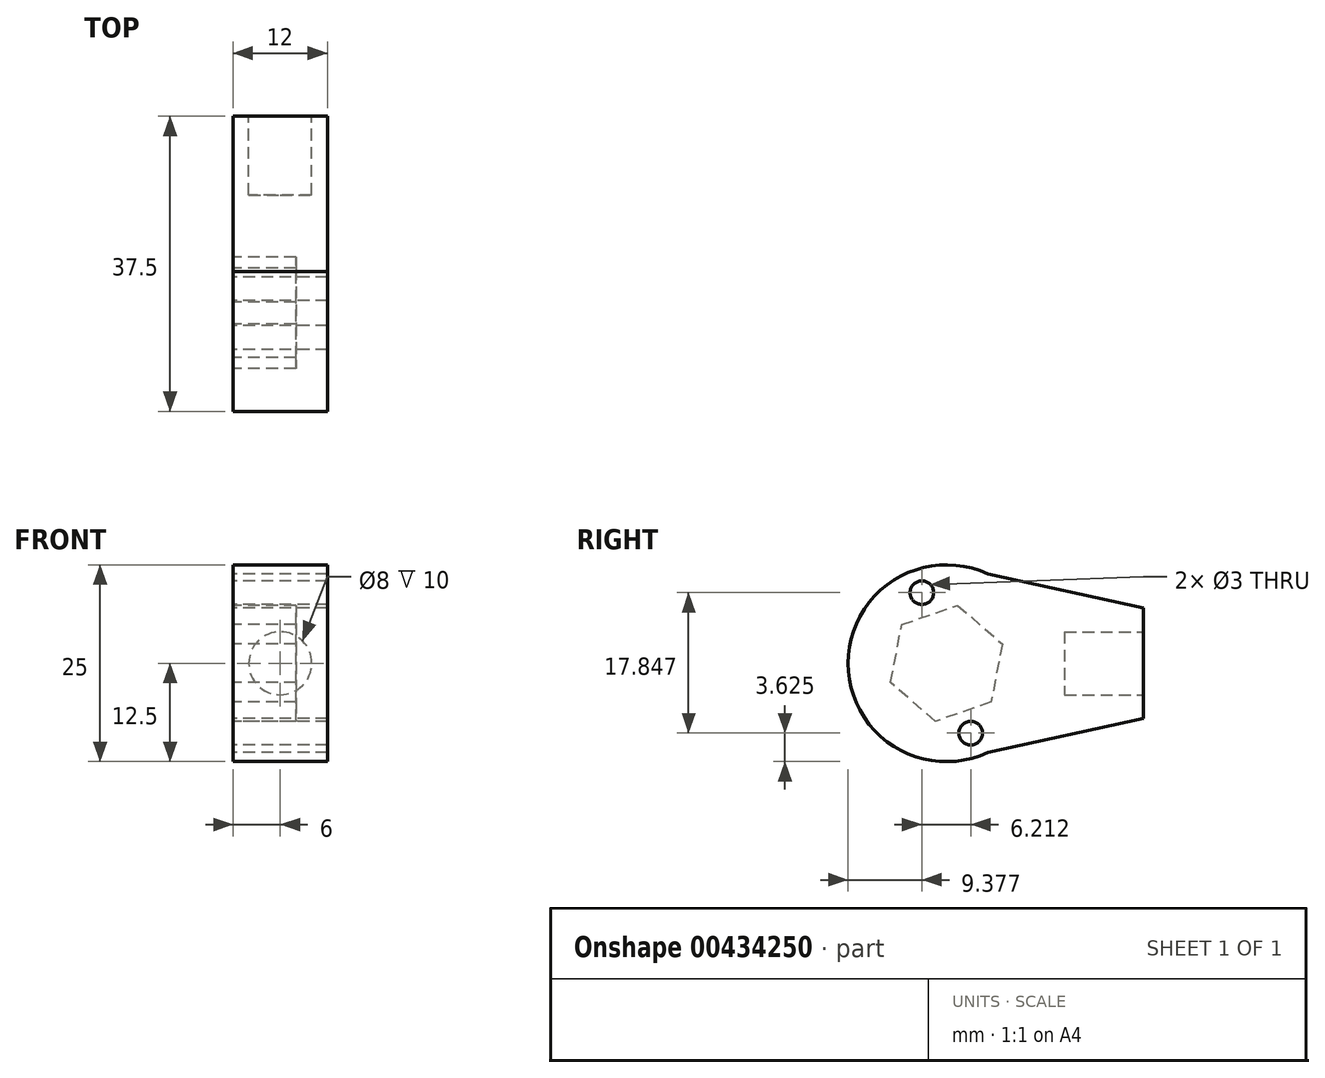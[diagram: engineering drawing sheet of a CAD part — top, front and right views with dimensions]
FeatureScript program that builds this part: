
annotation { "Feature Type Name" : "Feature", "Feature Type Description" : "" }
export const myFeature = defineFeature(function(context is Context, id is Id, definition is map)
    precondition{}
    {
        {
            var Q0;
            Q0=qCreatedBy(makeId("Right.planeOp"),FACE);
            var sketch = newSketch(context, id + "F0", { "sketchPlane" : qUnion([Q0])});
            skCircle(sketch, "E0", {"center": v(0, 0) * mm, "radius": 12.5 * mm});
            skCircle(sketch, "E1.cCircle", {"center": v(0, 0) * mm, "radius": 6.5 * mm, "construction": true});
            skLineSegment(sketch, "E1.0", {"start": v(5.68, -4.9) * mm, "end": v(-1.4, -7.37) * mm});
            skLineSegment(sketch, "E1.1", {"start": v(-1.4, -7.37) * mm, "end": v(-7.09, -2.47) * mm});
            skLineSegment(sketch, "E1.2", {"start": v(-7.09, -2.47) * mm, "end": v(-5.68, 4.9) * mm});
            skLineSegment(sketch, "E1.3", {"start": v(-5.68, 4.9) * mm, "end": v(1.4, 7.37) * mm});
            skLineSegment(sketch, "E1.4", {"start": v(1.4, 7.37) * mm, "end": v(7.09, 2.47) * mm});
            skLineSegment(sketch, "E1.5", {"start": v(7.09, 2.47) * mm, "end": v(5.68, -4.9) * mm});
            skPoint(sketch, "E1.0.midPoint", {"position": v(2.14, -6.14) * mm});
            skLineSegment(sketch, "E2", {"start": v(0, 0) * mm, "end": v(25, 0) * mm, "construction": true});
            skLineSegment(sketch, "E3", {"start": v(25, 0) * mm, "end": v(25, -7) * mm});
            skLineSegment(sketch, "E4.MirrorCS", {"start": v(25, 0) * mm, "end": v(25, 7) * mm});
            skLineSegment(sketch, "E5", {"start": v(0, -12.5) * mm, "end": v(25, -7) * mm});
            skLineSegment(sketch, "E6", {"start": v(0, 12.5) * mm, "end": v(25, 7) * mm});
            skSolve(sketch);
        }
        {
            var Q0;
            Q0 = qSketchRegion(id + "F0", true);
            extrude(context, id + "F1", {"entities" : qUnion([Q0]), "depth" : 12 * mm});
        }
        {
            var Q0;
            Q0=makeQuery(id+"F1.opExtrude","SWEPT_FACE",FACE,{"disambiguationData":[OSD([sQuery(id+"F0.wireOp",EDGE,"E3"),sQuery(id+"F0.wireOp",EDGE,"E4.MirrorCS")])]});
            var sketch = newSketch(context, id + "F2", { "sketchPlane" : qUnion([Q0])});
            skCircle(sketch, "E7", {"center": v(-6, 0) * mm, "radius": 4 * mm});
            skPoint(sketch, "E7.centerSnap0", {"position": v(-6, 7) * mm});
            skSolve(sketch);
        }
        {
            var Q0;
            Q0 = qSketchRegion(id + "F2", true);
            extrude(context, id + "F3", {"entities" : qUnion([Q0]), "operationType" : NewBodyOperationType.REMOVE, "oppositeDirection" : true, "depth" : 10 * mm});
        }
        {
            var Q0;
            Q0=makeQuery(id+"F1.opExtrude","CAP_FACE",FACE,{"disambiguationData":[OSD([sQuery(id+"F0.wireOp",EDGE,"E0"),sQuery(id+"F0.wireOp",EDGE,"E1.0"),sQuery(id+"F0.wireOp",EDGE,"E1.1"),sQuery(id+"F0.wireOp",EDGE,"E1.2"),sQuery(id+"F0.wireOp",EDGE,"E1.3"),sQuery(id+"F0.wireOp",EDGE,"E1.4"),sQuery(id+"F0.wireOp",EDGE,"E1.5"),sQuery(id+"F0.wireOp",EDGE,"E3"),sQuery(id+"F0.wireOp",EDGE,"E4.MirrorCS"),sQuery(id+"F0.wireOp",EDGE,"E5"),sQuery(id+"F0.wireOp",EDGE,"E6")])],"isStart":false});
            var sketch = newSketch(context, id + "F4", { "sketchPlane" : qUnion([Q0])});
            skCircle(sketch, "E8", {"center": v(0, 0) * mm, "radius": 7.55 * mm});
            skSolve(sketch);
        }
        {
            var Q0;
            Q0 = qSketchRegion(id + "F4", true);
            extrude(context, id + "F5", {"entities" : qUnion([Q0]), "operationType" : NewBodyOperationType.ADD, "oppositeDirection" : true, "depth" : 4 * mm});
        }
        {
            var Q0;
            Q0=makeQuery(id+"F1.opExtrude","CAP_FACE",FACE,{"disambiguationData":[OSD([sQuery(id+"F0.wireOp",EDGE,"E0"),sQuery(id+"F0.wireOp",EDGE,"E1.0"),sQuery(id+"F0.wireOp",EDGE,"E1.1"),sQuery(id+"F0.wireOp",EDGE,"E1.2"),sQuery(id+"F0.wireOp",EDGE,"E1.3"),sQuery(id+"F0.wireOp",EDGE,"E1.4"),sQuery(id+"F0.wireOp",EDGE,"E1.5"),sQuery(id+"F0.wireOp",EDGE,"E3"),sQuery(id+"F0.wireOp",EDGE,"E4.MirrorCS"),sQuery(id+"F0.wireOp",EDGE,"E5"),sQuery(id+"F0.wireOp",EDGE,"E6")])],"isStart":true});
            var sketch = newSketch(context, id + "F6", { "sketchPlane" : qUnion([Q0])});
            skLineSegment(sketch, "E9", {"start": v(2.14, 6.14) * mm, "end": v(4.1, 11.8) * mm, "construction": true});
            skLineSegment(sketch, "E10", {"start": v(-2.14, -6.14) * mm, "end": v(-4.04, -11.61) * mm, "construction": true});
            skCircle(sketch, "E11", {"center": v(3.12, 8.97) * mm, "radius": 1.5 * mm});
            skCircle(sketch, "E12", {"center": v(-3.09, -8.87) * mm, "radius": 1.5 * mm});
            skSolve(sketch);
        }
        {
            var Q0;
            Q0 = qSketchRegion(id + "F6", true);
            extrude(context, id + "F7", {"entities" : qUnion([Q0]), "operationType" : NewBodyOperationType.REMOVE, "oppositeDirection" : true, "depth" : 25 * mm});
        }
    });
